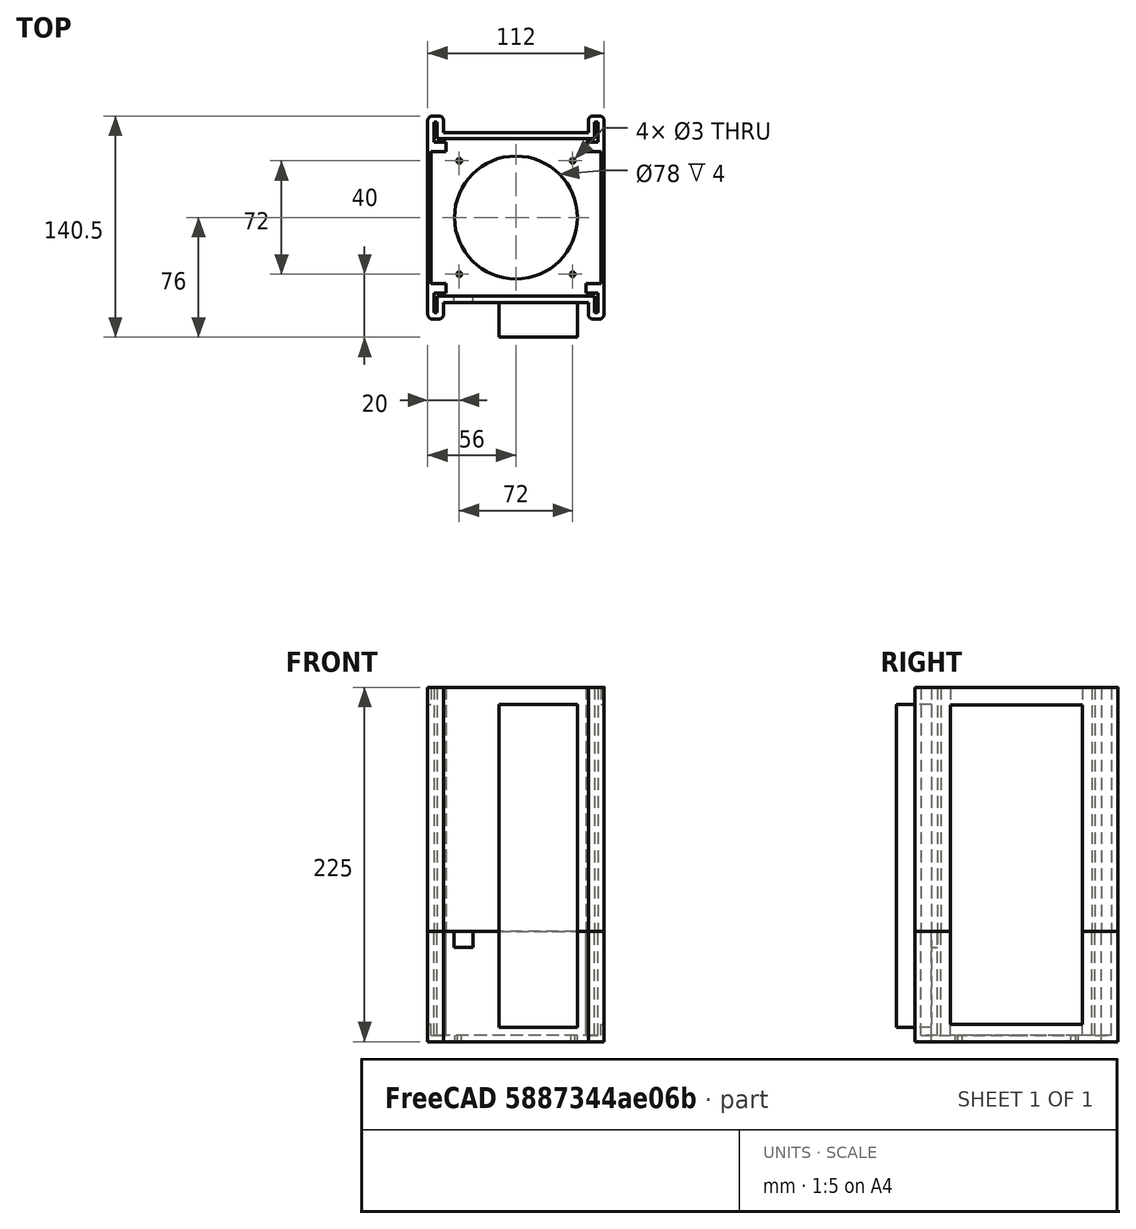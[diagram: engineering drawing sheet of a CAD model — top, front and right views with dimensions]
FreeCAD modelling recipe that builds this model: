
FCSTD DOCUMENT  (FreeCAD 0.21R33771 (Git))
Label: Conenctor Body
License: All rights reserved
LicenseURL: https://en.wikipedia.org/wiki/All_rights_reserved
objects: Mesh::Feature×9, Sketcher::SketchObject×7, PartDesign::Pad×4, PartDesign::Pocket×3, PartDesign::Body×3, PartDesign::Fillet×2
note: 28 computed .brp shape members not serialized (recipe doc carries the construction recipe); baked Part::Feature solids carry a one-line shape summary decoded from their .brp

FEATURE [Mesh::Feature] heat_sink_big
  Placement = pos=(-5,0,100) rot=(0,0,1;0rad)
FEATURE [Mesh::Feature] heat_sink_big001  label="heat_sink_big2"
  Placement = pos=(5,0,100) rot=(0,1,0;3.14159rad)
FEATURE [Mesh::Feature] heat_sink_big002  label="heat_sink_big3"
  Placement = pos=(5,0,200) rot=(0,1,0;3.14159rad)
FEATURE [Mesh::Feature] _x8_cm_12V_Fan_1742020218  label="8x8_cm_12V_Fan_1742020218"
  Placement = pos=(74,37,142) rot=(0,0,1;4.71239rad)
FEATURE [Mesh::Feature] _x8_cm_12V_Fan_1742020219  label="8x8_cm_12V_Fan_1742020219"
  Placement = pos=(74,37,41) rot=(0,0,1;4.71239rad)
FEATURE [Mesh::Feature] _x8_cm_12V_Fan_1742020220  label="8x8_cm_12V_Fan_1742020220"
  Placement = pos=(-70,37,41) rot=(0,0,1;4.71239rad)
FEATURE [Mesh::Feature] _x8_cm_12V_Fan_1742020221  label="8x8_cm_12V_Fan_1742020221"
  Placement = pos=(-70,37,142) rot=(0,0,1;4.71239rad)
FEATURE [Sketcher::SketchObject] Sketch002
  AttachmentOffset = pos=(0,0,4) rot=(0,0,1;0rad)
  FullyConstrained = true
  MapMode = 5
  Placement = pos=(0,0,4) rot=(0,0,1;0rad)
  Support = -> [XY_Plane002]
  sketch-geometry (40):
    g0: LineSegment StartX=-56 StartY=-10.5 StartZ=0 EndX=-46 EndY=-10.5 EndZ=0
    g1: LineSegment StartX=-46 StartY=-10.5 StartZ=0 EndX=-46 EndY=0 EndZ=0
    g2: LineSegment StartX=-46 StartY=0 StartZ=0 EndX=46 EndY=0 EndZ=0
    g3: LineSegment StartX=46 StartY=0 StartZ=0 EndX=46 EndY=-10.5 EndZ=0
    g4: LineSegment StartX=46 StartY=-10.5 StartZ=0 EndX=56 EndY=-10.5 EndZ=0
    g5: LineSegment StartX=52 StartY=6 StartZ=0 EndX=52 EndY=-6.5 EndZ=0
    g6: LineSegment StartX=52 StartY=-6.5 StartZ=0 EndX=50 EndY=-6.5 EndZ=0
    g7: LineSegment StartX=50 StartY=-6.5 StartZ=0 EndX=50 EndY=4 EndZ=0
    g8: LineSegment StartX=50 StartY=4 StartZ=0 EndX=-50 EndY=4 EndZ=0
    g9: LineSegment StartX=-50 StartY=4 StartZ=0 EndX=-50 EndY=-6.5 EndZ=0
    g10: LineSegment StartX=-50 StartY=-6.5 StartZ=0 EndX=-52 EndY=-6.5 EndZ=0
    g11: LineSegment StartX=-52 StartY=-6.5 StartZ=0 EndX=-52 EndY=6 EndZ=0
    g12: LineSegment StartX=-52 StartY=6 StartZ=0 EndX=-44.5 EndY=6 EndZ=0
    g13: LineSegment StartX=-44.5 StartY=6 StartZ=0 EndX=-44.5 EndY=12 EndZ=0
    g14: LineSegment StartX=52 StartY=6 StartZ=0 EndX=44.5 EndY=6 EndZ=0
    g15: LineSegment StartX=44.5 StartY=6 StartZ=0 EndX=44.5 EndY=12 EndZ=0
    g16: LineSegment StartX=-44.5 StartY=102 StartZ=0 EndX=-44.5 EndY=96 EndZ=0
    g17: LineSegment StartX=-56 StartY=118.5 StartZ=0 EndX=-46 EndY=118.5 EndZ=0
    g18: LineSegment StartX=-46 StartY=118.5 StartZ=0 EndX=-46 EndY=108 EndZ=0
    g19: LineSegment StartX=-46 StartY=108 StartZ=0 EndX=46 EndY=108 EndZ=0
    g20: LineSegment StartX=46 StartY=108 StartZ=0 EndX=46 EndY=118.5 EndZ=0
    g21: LineSegment StartX=46 StartY=118.5 StartZ=0 EndX=56 EndY=118.5 EndZ=0
    g22: LineSegment StartX=44.5 StartY=96 StartZ=0 EndX=44.5 EndY=102 EndZ=0
    g23: LineSegment StartX=44.5 StartY=102 StartZ=0 EndX=52 EndY=102 EndZ=0
    g24: LineSegment StartX=52 StartY=102 StartZ=0 EndX=52 EndY=114.5 EndZ=0
    g25: LineSegment StartX=52 StartY=114.5 StartZ=0 EndX=50 EndY=114.5 EndZ=0
    g26: LineSegment StartX=50 StartY=114.5 StartZ=0 EndX=50 EndY=104 EndZ=0
    g27: LineSegment StartX=50 StartY=104 StartZ=0 EndX=-50 EndY=104 EndZ=0
    g28: LineSegment StartX=-50 StartY=104 StartZ=0 EndX=-50 EndY=114.5 EndZ=0
    g29: LineSegment StartX=-50 StartY=114.5 StartZ=0 EndX=-52 EndY=114.5 EndZ=0
    g30: LineSegment StartX=-52 StartY=114.5 StartZ=0 EndX=-52 EndY=102 EndZ=0
    g31: LineSegment StartX=-52 StartY=102 StartZ=0 EndX=-44.5 EndY=102 EndZ=0
    g32: LineSegment StartX=-54 StartY=12 StartZ=0 EndX=-44.5 EndY=12 EndZ=0
    g33: LineSegment StartX=44.5 StartY=12 StartZ=0 EndX=54 EndY=12 EndZ=0
    g34: LineSegment StartX=44.5 StartY=96 StartZ=0 EndX=54 EndY=96 EndZ=0
    g35: LineSegment StartX=-54 StartY=96 StartZ=0 EndX=-44.5 EndY=96 EndZ=0
    g36: LineSegment StartX=-54 StartY=96 StartZ=0 EndX=-54 EndY=12 EndZ=0
    g37: LineSegment StartX=-56 StartY=-10.5 StartZ=0 EndX=-56 EndY=118.5 EndZ=0
    g38: LineSegment StartX=56 StartY=118.5 StartZ=0 EndX=56 EndY=-10.5 EndZ=0
    g39: LineSegment StartX=54 StartY=96 StartZ=0 EndX=54 EndY=12 EndZ=0
  constraints (120):
    c: Horizontal(g0)
    c: Coincident(g0,g1)
    c: Vertical(g1)
    c: Coincident(g1,g2)
    c: Horizontal(g2)
    c: Coincident(g2,g3)
    c: Vertical(g3)
    c: Coincident(g3,g4)
    c: Horizontal(g4)
    c: Vertical(g5)
    c: Coincident(g5,g6)
    c: Coincident(g6,g7)
    c: Vertical(g7)
    c: Coincident(g7,g8)
    c: Horizontal(g8)
    c: Coincident(g8,g9)
    c: Vertical(g9)
    c: Coincident(g9,g10)
    c: Horizontal(g10)
    c: Coincident(g10,g11)
    c: Vertical(g11)
    c: DistanceX(g10,g10) = 2
    c: DistanceY(g1,g8) = 4
    c: DistanceX(g8,g1) = 4
    c: DistanceY(g9,g9) = 10.5
    c: DistanceY(g0,g10) = 4
    c: Horizontal(g12)
    c: Coincident(g12,g13)
    c: Vertical(g13)
    c: DistanceX(g12,g12) = 7.5
    c: DistanceY(g13,g13) = 6
    c: DistanceY(g8,g12) = 2
    c: Coincident(g11,g12)
    c: Coincident(g14,g15)
    c: Coincident(g5,g14)
    c: Vertical(g16)
    c: Horizontal(g17)
    c: Coincident(g17,g18)
    c: Vertical(g18)
    c: Coincident(g18,g19)
    c: Horizontal(g19)
    c: Coincident(g19,g20)
    c: Vertical(g20)
    c: Coincident(g20,g21)
    c: Horizontal(g21)
    c: Coincident(g22,g23)
    c: Horizontal(g23)
    c: Coincident(g23,g24)
    c: Coincident(g24,g25)
    c: Horizontal(g25)
    c: Coincident(g25,g26)
    c: Coincident(g26,g27)
    c: Horizontal(g27)
    c: Coincident(g27,g28)
    c: Vertical(g28)
    c: Coincident(g28,g29)
    c: Coincident(g29,g30)
    c: Vertical(g30)
    c: Coincident(g30,g31)
    c: Coincident(g31,g16)
    c: Horizontal(g31)
    c: Vertical(g22)
    c: Horizontal(g29)
    c: DistanceX(g29,g29) = 2
    c: DistanceY(g22,g22) = 6
    c: DistanceY(g23,g26) = 2
    c: DistanceY(g25,g20) = 4
    c: DistanceX(g17,g29) = 4
    c: DistanceY(g29,g17) = 4
    c: DistanceX(g28,g17) = 4
    c: DistanceY(g16,g27) = 2
    c: Equal(g18,g1)
    c: DistanceY(g27,g18) = 4
    c: Equal(g20,g18)
    c: Coincident(g32,g13)
    c: Horizontal(g32)
    c: Coincident(g33,g15)
    c: Coincident(g34,g22)
    c: Horizontal(g34)
    c: Coincident(g35,g16)
    c: Horizontal(g35)
    c: Equal(g8,g27)
    c: DistanceX(g27,g27) = 100
    c: Vertical(g36)
    c: Coincident(g32,g36)
    c: Coincident(g37,g0)
    c: Coincident(g37,g17)
    c: Vertical(g37)
    c: DistanceX(g0,g0) = 10
    c: DistanceX(g0,g32) = 2
    c: Equal(g32,g35)
    c: Coincident(g35,g36)
    c: Coincident(g38,g21)
    c: Coincident(g38,g4)
    c: Vertical(g38)
    c: Coincident(g39,g34)
    c: Coincident(g39,g33)
    c: Vertical(g39)
    c: DistanceY(g-1,g13) = 12
    c: DistanceX(g12,g-1) = 44.5
    c: DistanceX(g-1,g14) = 44.5
    c: Equal(g32,g33)
    c: Vertical(g15)
    c: DistanceX(g33,g4) = 2
    c: Horizontal(g0,g3)
    c: DistanceX(g4,g4) = 10
    c: Vertical(g24)
    c: DistanceY(g16,g16) = 6
    c: Equal(g11,g5)
    c: Equal(g10,g6)
    c: Horizontal(g33)
    c: Horizontal(g14)
    c: Horizontal(g14,g12)
    c: Horizontal(g15,g13)
    c: Equal(g29,g25)
    c: Vertical(g26)
    c: Equal(g34,g35)
    c: Equal(g2,g19)
    c: Horizontal(g6)
    c: DistanceY(g7,g26) = 100
FEATURE [Sketcher::SketchObject] Sketch004
  AttachmentOffset = pos=(0,0,4) rot=(0,0,1;0rad)
  FullyConstrained = true
  MapMode = 5
  Placement = pos=(0,0,4) rot=(0,0,1;0rad)
  Support = -> [XY_Plane003]
  sketch-geometry (40):
    g0: LineSegment StartX=-56 StartY=-12 StartZ=0 EndX=-46 EndY=-12 EndZ=0
    g1: LineSegment StartX=-46 StartY=-12 StartZ=0 EndX=-46 EndY=-1.5 EndZ=0
    g2: LineSegment StartX=-46 StartY=-1.5 StartZ=0 EndX=46 EndY=-1.5 EndZ=0
    g3: LineSegment StartX=46 StartY=-1.5 StartZ=0 EndX=46 EndY=-12 EndZ=0
    g4: LineSegment StartX=46 StartY=-12 StartZ=0 EndX=56 EndY=-12 EndZ=0
    g5: LineSegment StartX=52 StartY=4.5 StartZ=0 EndX=52 EndY=-8 EndZ=0
    g6: LineSegment StartX=52 StartY=-8 StartZ=0 EndX=50 EndY=-8 EndZ=0
    g7: LineSegment StartX=50 StartY=-8 StartZ=0 EndX=50 EndY=2.5 EndZ=0
    g8: LineSegment StartX=50 StartY=2.5 StartZ=0 EndX=-50 EndY=2.5 EndZ=0
    g9: LineSegment StartX=-50 StartY=2.5 StartZ=0 EndX=-50 EndY=-8 EndZ=0
    g10: LineSegment StartX=-50 StartY=-8 StartZ=0 EndX=-52 EndY=-8 EndZ=0
    g11: LineSegment StartX=-52 StartY=-8 StartZ=0 EndX=-52 EndY=4.5 EndZ=0
    g12: LineSegment StartX=-52 StartY=4.5 StartZ=0 EndX=-44.5 EndY=4.5 EndZ=0
    g13: LineSegment StartX=-44.5 StartY=4.5 StartZ=0 EndX=-44.5 EndY=10.5 EndZ=0
    g14: LineSegment StartX=52 StartY=4.5 StartZ=0 EndX=44.5 EndY=4.5 EndZ=0
    g15: LineSegment StartX=44.5 StartY=4.5 StartZ=0 EndX=44.5 EndY=10.5 EndZ=0
    g16: LineSegment StartX=-44.5 StartY=100.5 StartZ=0 EndX=-44.5 EndY=94.5 EndZ=0
    g17: LineSegment StartX=-56 StartY=117 StartZ=0 EndX=-46 EndY=117 EndZ=0
    g18: LineSegment StartX=-46 StartY=117 StartZ=0 EndX=-46 EndY=106.5 EndZ=0
    g19: LineSegment StartX=-46 StartY=106.5 StartZ=0 EndX=46 EndY=106.5 EndZ=0
    g20: LineSegment StartX=46 StartY=106.5 StartZ=0 EndX=46 EndY=117 EndZ=0
    g21: LineSegment StartX=46 StartY=117 StartZ=0 EndX=56 EndY=117 EndZ=0
    g22: LineSegment StartX=44.5 StartY=94.5 StartZ=0 EndX=44.5 EndY=100.5 EndZ=0
    g23: LineSegment StartX=44.5 StartY=100.5 StartZ=0 EndX=52 EndY=100.5 EndZ=0
    g24: LineSegment StartX=52 StartY=100.5 StartZ=0 EndX=52 EndY=113 EndZ=0
    g25: LineSegment StartX=52 StartY=113 StartZ=0 EndX=50 EndY=113 EndZ=0
    g26: LineSegment StartX=50 StartY=113 StartZ=0 EndX=50 EndY=102.5 EndZ=0
    g27: LineSegment StartX=50 StartY=102.5 StartZ=0 EndX=-50 EndY=102.5 EndZ=0
    g28: LineSegment StartX=-50 StartY=102.5 StartZ=0 EndX=-50 EndY=113 EndZ=0
    g29: LineSegment StartX=-50 StartY=113 StartZ=0 EndX=-52 EndY=113 EndZ=0
    g30: LineSegment StartX=-52 StartY=113 StartZ=0 EndX=-52 EndY=100.5 EndZ=0
    g31: LineSegment StartX=-52 StartY=100.5 StartZ=0 EndX=-44.5 EndY=100.5 EndZ=0
    g32: LineSegment StartX=-54 StartY=10.5 StartZ=0 EndX=-44.5 EndY=10.5 EndZ=0
    g33: LineSegment StartX=44.5 StartY=94.5 StartZ=0 EndX=54 EndY=94.5 EndZ=0
    g34: LineSegment StartX=-54 StartY=94.5 StartZ=0 EndX=-44.5 EndY=94.5 EndZ=0
    g35: LineSegment StartX=-54 StartY=94.5 StartZ=0 EndX=-54 EndY=10.5 EndZ=0
    g36: LineSegment StartX=-56 StartY=-12 StartZ=0 EndX=-56 EndY=117 EndZ=0
    g37: LineSegment StartX=56 StartY=117 StartZ=0 EndX=56 EndY=-12 EndZ=0
    g38: LineSegment StartX=54 StartY=10.5 StartZ=0 EndX=54 EndY=94.5 EndZ=0
    g39: LineSegment StartX=44.5 StartY=10.5 StartZ=0 EndX=54 EndY=10.5 EndZ=0
  constraints (121):
    c: Horizontal(g0)
    c: Coincident(g0,g1)
    c: Vertical(g1)
    c: Coincident(g1,g2)
    c: Horizontal(g2)
    c: Coincident(g2,g3)
    c: Vertical(g3)
    c: Coincident(g3,g4)
    c: Horizontal(g4)
    c: Vertical(g5)
    c: Coincident(g5,g6)
    c: Coincident(g6,g7)
    c: Vertical(g7)
    c: Coincident(g7,g8)
    c: Horizontal(g8)
    c: Coincident(g8,g9)
    c: Vertical(g9)
    c: Coincident(g9,g10)
    c: Horizontal(g10)
    c: Coincident(g10,g11)
    c: Vertical(g11)
    c: Horizontal(g6)
    c: DistanceX(g10,g10) = 2
    c: DistanceX(g6,g6) = 2
    c: DistanceY(g1,g8) = 4
    c: DistanceX(g8,g1) = 4
    c: DistanceX(g2,g7) = 4
    c: DistanceY(g9,g9) = 10.5
    c: DistanceY(g7,g7) = 10.5
    c: DistanceY(g0,g10) = 4
    c: DistanceY(g3,g6) = 4
    c: Horizontal(g12)
    c: Coincident(g12,g13)
    c: Vertical(g13)
    c: DistanceX(g12,g12) = 7.5
    c: DistanceY(g13,g13) = 6
    c: DistanceY(g8,g12) = 2
    c: Coincident(g11,g12)
    c: Coincident(g14,g15)
    c: Horizontal(g14)
    c: Vertical(g15)
    c: DistanceY(g7,g5) = 2
    c: DistanceX(g14,g14) = 7.5
    c: DistanceY(g15,g15) = 6
    c: Coincident(g5,g14)
    c: Vertical(g16)
    c: Horizontal(g17)
    c: Coincident(g17,g18)
    c: Vertical(g18)
    c: Coincident(g18,g19)
    c: Horizontal(g19)
    c: Coincident(g19,g20)
    c: Vertical(g20)
    c: Coincident(g20,g21)
    c: Horizontal(g21)
    c: Coincident(g22,g23)
    c: Horizontal(g23)
    c: Coincident(g23,g24)
    c: Vertical(g24)
    c: Coincident(g24,g25)
    c: Horizontal(g25)
    c: Coincident(g25,g26)
    c: Vertical(g26)
    c: Coincident(g26,g27)
    c: Horizontal(g27)
    c: Coincident(g27,g28)
    c: Vertical(g28)
    c: Coincident(g28,g29)
    c: Coincident(g29,g30)
    c: Vertical(g30)
    c: Coincident(g30,g31)
    c: Coincident(g31,g16)
    c: Horizontal(g31)
    c: Vertical(g22)
    c: Horizontal(g29)
    c: Equal(g29,g25)
    c: DistanceX(g29,g29) = 2
    c: Equal(g16,g22)
    c: DistanceY(g22,g22) = 6
    c: DistanceY(g23,g26) = 2
    c: DistanceX(g24,g21) = 4
    c: DistanceX(g20,g25) = 4
    c: DistanceY(g25,g20) = 4
    c: DistanceX(g17,g29) = 4
    c: DistanceY(g29,g17) = 4
    c: DistanceX(g28,g17) = 4
    c: DistanceY(g16,g27) = 2
    c: Equal(g18,g1)
    c: DistanceY(g27,g18) = 4
    c: Equal(g20,g18)
    c: DistanceY(g8,g27) = 100
    c: Coincident(g32,g13)
    c: Horizontal(g32)
    c: Coincident(g33,g22)
    c: Horizontal(g33)
    c: Coincident(g34,g16)
    c: Horizontal(g34)
    c: DistanceX(g8,g8) = 100
    c: DistanceX(g12,g-1) = 44.5
    c: DistanceY(g1,g-1) = 1.5
    c: Vertical(g35)
    c: Vertical(g36)
    c: Vertical(g37)
    c: Vertical(g38)
    c: DistanceX(g36,g35) = 2
    c: DistanceX(g38,g37) = 2
    c: Coincident(g32,g35)
    c: Coincident(g39,g15)
    c: Coincident(g39,g38)
    c: Horizontal(g39)
    c: Equal(g32,g39)
    c: DistanceX(g32,g32) = 9.5
    c: Coincident(g34,g35)
    c: Equal(g31,g23)
    c: Equal(g34,g33)
    c: Equal(g38,g35)
    c: Coincident(g0,g36)
    c: Coincident(g17,g36)
    c: Coincident(g4,g37)
    c: Coincident(g21,g37)
    c: Equal(g34,g32)
FEATURE [PartDesign::Pad] Pad
  Direction = (0,0,1)
  Length = 66
  Length2 = 10
  Profile = -> Sketch002
  ReferenceAxis = -> Sketch002 [N_Axis]
  Type = 0
FEATURE [Mesh::Feature] _x8_cm_12V_Fan_1742020222  label="8x8_cm_12V_Fan_1742020222"
  Placement = pos=(10,37,-16) rot=(0.57735,-0.57735,-0.57735;2.0944rad)
FEATURE [Sketcher::SketchObject] Sketch
  AttachmentOffset = pos=(0,0,70) rot=(0,0,1;0rad)
  ExternalGeometry = -> [Pad]
  FullyConstrained = false
  MapMode = 5
  Placement = pos=(0,0,70) rot=(0,0,1;0rad)
  Support = -> [XY_Plane002]
  sketch-geometry (4):
    g0: LineSegment StartX=-61.9532 StartY=96 StartZ=0 EndX=58.0468 EndY=96 EndZ=0
    g1: LineSegment StartX=58.0468 StartY=96 StartZ=0 EndX=58.0468 EndY=12 EndZ=0
    g2: LineSegment StartX=58.0468 StartY=12 StartZ=0 EndX=-61.9532 EndY=12 EndZ=0
    g3: LineSegment StartX=-61.9532 StartY=12 StartZ=0 EndX=-61.9532 EndY=96 EndZ=0
  constraints (11):
    c: Coincident(g0,g1)
    c: Coincident(g1,g2)
    c: Coincident(g2,g3)
    c: Coincident(g3,g0)
    c: Horizontal(g0)
    c: Horizontal(g2)
    c: Vertical(g1)
    c: Vertical(g3)
    c: PointOnObject(g-4,g2)
    c: PointOnObject(g-3,g0)
    c: DistanceX(g0,g0) = 120
FEATURE [PartDesign::Pocket] Pocket002
  BaseFeature = -> Pad
  Direction = (0,0,-1)
  Length = 59
  Length2 = 5
  Profile = -> Sketch
  ReferenceAxis = -> Sketch [N_Axis]
  Type = 0
FEATURE [Sketcher::SketchObject] Sketch009  label="air_inlet"
  ExternalGeometry = -> [Pocket002]
  FullyConstrained = true
  MapMode = 5
  Support = -> [XY_Plane002]
  sketch-geometry (17):
    g0: LineSegment StartX=-56 StartY=118.5 StartZ=0 EndX=-46 EndY=118.5 EndZ=0
    g1: LineSegment StartX=-46 StartY=118.5 StartZ=0 EndX=-46 EndY=108 EndZ=0
    g2: LineSegment StartX=-46 StartY=108 StartZ=0 EndX=46 EndY=108 EndZ=0
    g3: LineSegment StartX=46 StartY=108 StartZ=0 EndX=46 EndY=118.5 EndZ=0
    g4: LineSegment StartX=46 StartY=118.5 StartZ=0 EndX=56 EndY=118.5 EndZ=0
    g5: LineSegment StartX=56 StartY=118.5 StartZ=0 EndX=56 EndY=-10.5 EndZ=0
    g6: LineSegment StartX=56 StartY=-10.5 StartZ=0 EndX=46 EndY=-10.5 EndZ=0
    g7: LineSegment StartX=46 StartY=-10.5 StartZ=0 EndX=46 EndY=0 EndZ=0
    g8: LineSegment StartX=46 StartY=0 StartZ=0 EndX=-46 EndY=0 EndZ=0
    g9: LineSegment StartX=-46 StartY=0 StartZ=0 EndX=-46 EndY=-10.5 EndZ=0
    g10: LineSegment StartX=-46 StartY=-10.5 StartZ=0 EndX=-56 EndY=-10.5 EndZ=0
    g11: LineSegment StartX=-56 StartY=-10.5 StartZ=0 EndX=-56 EndY=118.5 EndZ=0
    g12: Circle CenterX=0 CenterY=54 CenterZ=0 NormalX=0 NormalY=0 NormalZ=1 AngleXU=0 Radius=39
    g13: Circle CenterX=36 CenterY=90 CenterZ=0 NormalX=0 NormalY=0 NormalZ=1 AngleXU=0 Radius=1.5
    g14: Circle CenterX=-36 CenterY=90 CenterZ=0 NormalX=0 NormalY=0 NormalZ=1 AngleXU=0 Radius=1.5
    g15: Circle CenterX=-36 CenterY=18 CenterZ=0 NormalX=0 NormalY=0 NormalZ=1 AngleXU=0 Radius=1.5
    g16: Circle CenterX=36 CenterY=18 CenterZ=0 NormalX=0 NormalY=0 NormalZ=1 AngleXU=0 Radius=1.5
  constraints (39):
    c: Coincident(g-3,g0)
    c: Coincident(g0,g-3)
    c: Coincident(g0,g1)
    c: Coincident(g1,g-7)
    c: Coincident(g1,g2)
    c: Coincident(g2,g-7)
    c: Coincident(g2,g3)
    c: Coincident(g3,g-4)
    c: Coincident(g3,g4)
    c: Coincident(g4,g-4)
    c: Coincident(g4,g5)
    c: Coincident(g5,g-5)
    c: Coincident(g5,g6)
    c: Coincident(g6,g-5)
    c: Coincident(g6,g7)
    c: Coincident(g7,g-8)
    c: Coincident(g7,g8)
    c: Coincident(g8,g-8)
    c: Coincident(g8,g9)
    c: Coincident(g9,g-6)
    c: Coincident(g9,g10)
    c: Coincident(g10,g-6)
    c: Coincident(g10,g11)
    c: Coincident(g11,g0)
    c: PointOnObject(g12,g-2)
    c: Diameter(g12) = 78
    c: Diameter(g16) = 3
    c: Diameter(g14) = 3
    c: Diameter(g15) = 3
    c: Horizontal(g13,g14)
    c: Vertical(g14,g15)
    c: Horizontal(g15,g16)
    c: Vertical(g16,g13)
    c: DistanceX(g14,g13) = 72
    c: DistanceY(g15,g14) = 72
    c: Diameter(g13) = 3
    c: DistanceX(g15,g12) = 36
    c: DistanceY(g12,g13) = 36
    c: DistanceY(g12,g2) = 54
FEATURE [PartDesign::Pad] Pad008
  BaseFeature = -> Pocket002
  Direction = (0,0,1)
  Length = 4
  Length2 = 10
  Profile = -> Sketch009
  ReferenceAxis = -> Sketch009 [N_Axis]
  Type = 0
FEATURE [Mesh::Feature] heat_sink_big003
  Placement = pos=(-5,0,0) rot=(0,0,1;0rad)
FEATURE [PartDesign::Pad] Pad009
  Direction = (0,0,1)
  Length = 155
  Length2 = 10
  Profile = -> Sketch004
  ReferenceAxis = -> Sketch004 [N_Axis]
  Type = 0
FEATURE [Sketcher::SketchObject] Sketch010
  AttachmentOffset = pos=(0,0,170) rot=(0,0,1;0rad)
  ExternalGeometry = -> [Pad009]
  FullyConstrained = false
  MapMode = 5
  Placement = pos=(0,0,170) rot=(0,0,1;0rad)
  Support = -> [XY_Plane003]
  sketch-geometry (4):
    g0: LineSegment StartX=-70.6926 StartY=94.5 StartZ=0 EndX=63.138 EndY=94.5 EndZ=0
    g1: LineSegment StartX=63.138 StartY=94.5 StartZ=0 EndX=63.138 EndY=10.5 EndZ=0
    g2: LineSegment StartX=63.138 StartY=10.5 StartZ=0 EndX=-70.6926 EndY=10.5 EndZ=0
    g3: LineSegment StartX=-70.6926 StartY=10.5 StartZ=0 EndX=-70.6926 EndY=94.5 EndZ=0
  constraints (10):
    c: Coincident(g0,g1)
    c: Coincident(g1,g2)
    c: Coincident(g2,g3)
    c: Coincident(g3,g0)
    c: Horizontal(g0)
    c: Horizontal(g2)
    c: Vertical(g1)
    c: Vertical(g3)
    c: PointOnObject(g-4,g2)
    c: PointOnObject(g-3,g0)
FEATURE [PartDesign::Pocket] Pocket
  BaseFeature = -> Pad009
  Direction = (0,0,-1)
  Length = 155
  Length2 = 5
  Profile = -> Sketch010
  ReferenceAxis = -> Sketch010 [N_Axis]
  Type = 0
FEATURE [PartDesign::Fillet] Fillet
  Base = -> Pocket [Edge100,Edge99,Edge96,Edge8,Edge104,Edge105,Edge48,Edge2]
  BaseFeature = -> Pocket
  Radius = 3
  SupportTransform = false
  UseAllEdges = false
FEATURE [PartDesign::Body] Body003  label="bottom"
  Group = -> [Sketch004,Pad009,Sketch010,Pocket,Fillet]
  Origin = -> Origin003
  Placement = pos=(0,106.5,215) rot=(1,0,0;3.14159rad)
  Tip = -> Fillet
FEATURE [PartDesign::Fillet] Fillet001
  Base = -> Pad008 [Edge2,Edge12,Edge85,Edge87,Edge61,Edge8,Edge155,Edge90]
  BaseFeature = -> Pad008
  Radius = 3
  SupportTransform = false
  UseAllEdges = false
FEATURE [Sketcher::SketchObject] Sketch011
  FullyConstrained = false
  MapMode = 5
  Placement = pos=(0,0,0) rot=(1,0,0;1.5708rad)
  Support = -> [XZ_Plane]
  sketch-geometry (4):
    g0: LineSegment StartX=-10.8893 StartY=200.128 StartZ=0 EndX=39.1107 EndY=200.128 EndZ=0
    g1: LineSegment StartX=39.1107 StartY=200.128 StartZ=0 EndX=39.1107 EndY=-4.87168 EndZ=0
    g2: LineSegment StartX=39.1107 StartY=-4.87168 StartZ=0 EndX=-10.8893 EndY=-4.87168 EndZ=0
    g3: LineSegment StartX=-10.8893 StartY=-4.87168 StartZ=0 EndX=-10.8893 EndY=200.128 EndZ=0
  constraints (10):
    c: Coincident(g0,g1)
    c: Coincident(g1,g2)
    c: Coincident(g2,g3)
    c: Coincident(g3,g0)
    c: Horizontal(g0)
    c: Horizontal(g2)
    c: Vertical(g1)
    c: Vertical(g3)
    c: DistanceY(g1,g1) = 205
    c: DistanceX(g2,g2) = 50
FEATURE [PartDesign::Pad] Pad010
  Direction = (0,-1,2e-16)
  Length = 22
  Length2 = 10
  Placement = pos=(0,0,0) rot=(1,0,0;1.5708rad)
  Profile = -> Sketch011
  ReferenceAxis = -> Sketch011 [N_Axis]
  Type = 0
FEATURE [PartDesign::Body] Body
  Group = -> [Sketch011,Pad010]
  Origin = -> Origin
  Tip = -> Pad010
FEATURE [Sketcher::SketchObject] Sketch012
  ExternalGeometry = -> [Fillet001]
  FullyConstrained = false
  MapMode = 5
  Placement = pos=(0,0,0) rot=(1,0,0;1.5708rad)
  Support = -> [XZ_Plane002]
  sketch-geometry (4):
    g0: LineSegment StartX=-39.3031 StartY=70 StartZ=0 EndX=-27.3031 EndY=70 EndZ=0
    g1: LineSegment StartX=-27.3031 StartY=70 StartZ=0 EndX=-27.3031 EndY=60 EndZ=0
    g2: LineSegment StartX=-27.3031 StartY=60 StartZ=0 EndX=-39.3031 EndY=60 EndZ=0
    g3: LineSegment StartX=-39.3031 StartY=60 StartZ=0 EndX=-39.3031 EndY=70 EndZ=0
  constraints (11):
    c: Coincident(g0,g1)
    c: Coincident(g1,g2)
    c: Coincident(g2,g3)
    c: Coincident(g3,g0)
    c: Horizontal(g0)
    c: Horizontal(g2)
    c: Vertical(g1)
    c: Vertical(g3)
    c: PointOnObject(g0,g-3)
    c: DistanceY(g1,g1) = 10
    c: DistanceX(g2,g2) = 12
FEATURE [PartDesign::Pocket] Pocket003
  BaseFeature = -> Fillet001
  Direction = (0,1,2e-16)
  Length = 8
  Length2 = 5
  Profile = -> Sketch012
  ReferenceAxis = -> Sketch012 [N_Axis]
  Type = 0
FEATURE [PartDesign::Body] Body002  label="top"
  Group = -> [Sketch002,Pad,Sketch,Pocket002,Sketch009,Pad008,Fillet001,Sketch012,Pocket003]
  Origin = -> Origin002
  Placement = pos=(0,0,-14) rot=(0,0,1;0rad)
  Tip = -> Pocket003
